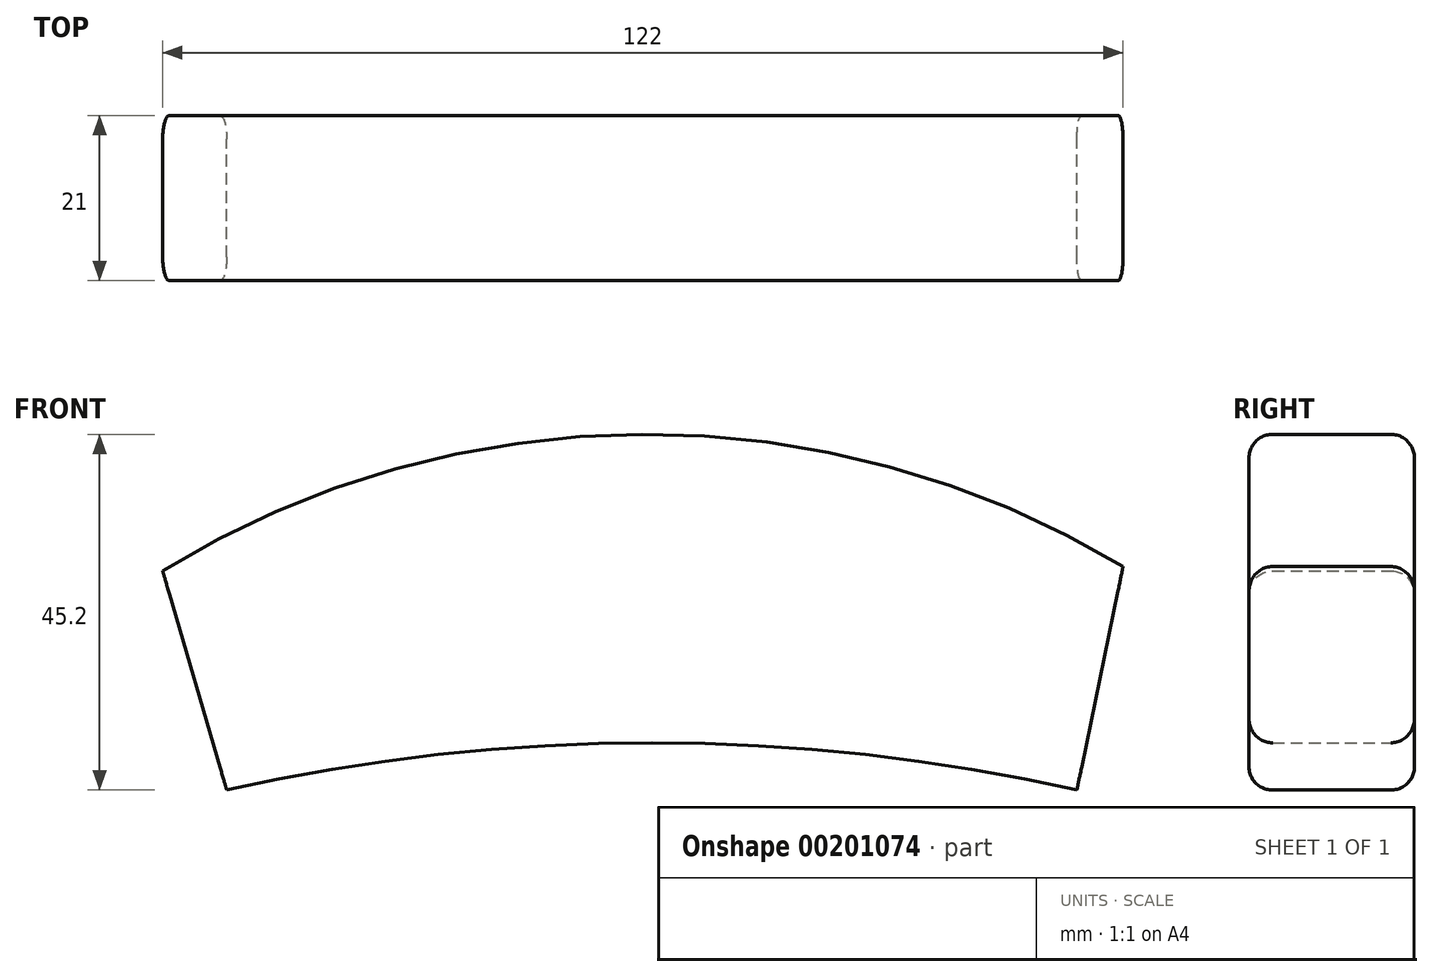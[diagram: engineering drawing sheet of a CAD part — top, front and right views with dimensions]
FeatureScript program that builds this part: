
annotation { "Feature Type Name" : "Feature", "Feature Type Description" : "" }
export const myFeature = defineFeature(function(context is Context, id is Id, definition is map)
    precondition{}
    {
        {
            var Q0;
            Q0=qCreatedBy(makeId("Front.planeOp"),FACE);
            var sketch = newSketch(context, id + "F0", { "sketchPlane" : qUnion([Q0])});
            skLineSegment(sketch, "E0", {"start": v(60.73, -16.42) * mm, "end": v(54.86, -44.82) * mm});
            skLineSegment(sketch, "E1", {"start": v(-61.27, -16.98) * mm, "end": v(-53.14, -44.82) * mm});
            skArc(sketch, "E2", {"start": v(60.73, -16.42) * mm, "mid": v(-0.35, 0.38) * mm, "end": v(-61.27, -16.98) * mm});
            skArc(sketch, "E3", {"start": v(54.86, -44.82) * mm, "mid": v(0.86, -38.82) * mm, "end": v(-53.14, -44.82) * mm});
            skSolve(sketch);
        }
        {
            var Q0;
            Q0=makeQuery(id+"F0.imprint","IMPRINT",FACE,{"disambiguationData":[TD([[makeQuery(id+"F0.imprint","IMPRINT",EDGE,{"derivedFrom":sQuery(id+"F0.wireOp",EDGE,"E0")}),-1.0]])]});
            extrude(context, id + "F1", {"entities" : qUnion([Q0]), "depth" : 21 * mm});
        }
        {
            var Q0;
            Q0=makeQuery(id+"F1.opExtrude","CAP_EDGE",EDGE,{"disambiguationData":[OSD([sQuery(id+"F0.wireOp",EDGE,"E2")])],"isStart":false});
            fillet(context, id + "F2", {"entities" : qUnion([Q0]), "radius" : 3 * mm, "tangentPropagation" : true, "allowEdgeOverflow" : false});
        }
        {
            var Q0;
            Q0=makeQuery(id+"F1.opExtrude","CAP_EDGE",EDGE,{"disambiguationData":[OSD([sQuery(id+"F0.wireOp",EDGE,"E2")])],"isStart":true});
            var Q1;
            Q1=makeQuery(id+"F1.opExtrude","CAP_EDGE",EDGE,{"disambiguationData":[OSD([sQuery(id+"F0.wireOp",EDGE,"E3")])],"isStart":false});
            var Q2;
            Q2=makeQuery(id+"F1.opExtrude","CAP_EDGE",EDGE,{"disambiguationData":[OSD([sQuery(id+"F0.wireOp",EDGE,"E3")])],"isStart":true});
            fillet(context, id + "F3", {"entities" : qUnion([Q0, Q1, Q2]), "radius" : 3 * mm, "tangentPropagation" : true, "allowEdgeOverflow" : false});
        }
    });
